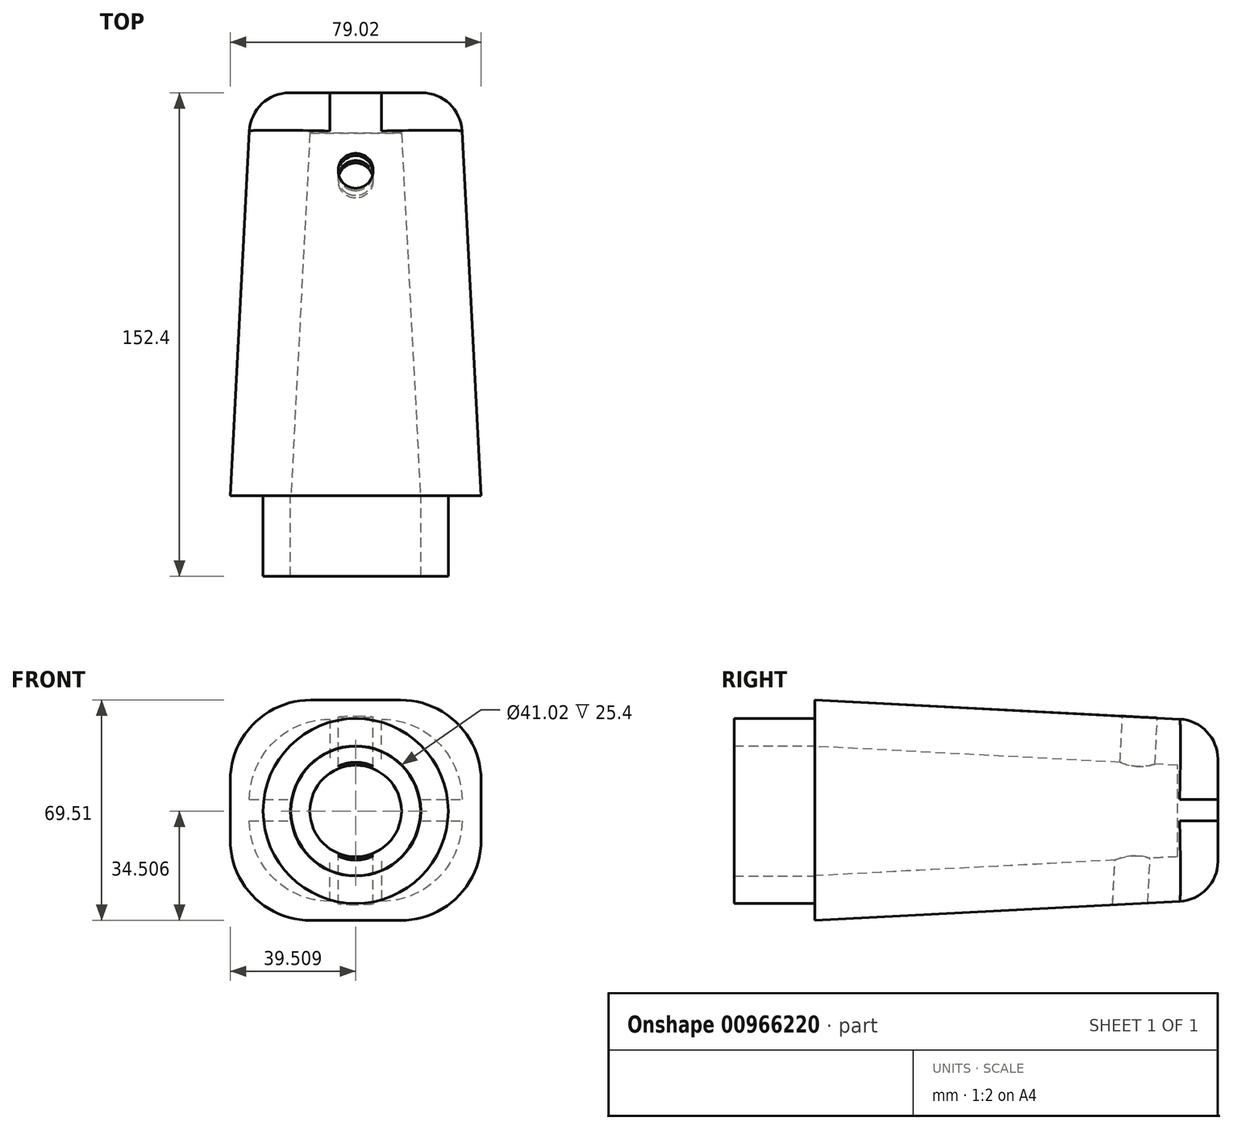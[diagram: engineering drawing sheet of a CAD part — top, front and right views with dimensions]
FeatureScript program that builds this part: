
annotation { "Feature Type Name" : "Feature", "Feature Type Description" : "" }
export const myFeature = defineFeature(function(context is Context, id is Id, definition is map)
    precondition{}
    {
        {
            var Q0;
            Q0=qCreatedBy(makeId("Front.planeOp"),FACE);
            var sketch = newSketch(context, id + "F0", { "sketchPlane" : qUnion([Q0])});
            skLineSegment(sketch, "E0.bottom", {"start": v(-78.57, 0) * mm, "end": v(-144.29, 0) * mm});
            skLineSegment(sketch, "E0.top", {"start": v(-78.57, 56.2) * mm, "end": v(-144.29, 56.2) * mm});
            skLineSegment(sketch, "E0.left", {"start": v(-78.57, 0) * mm, "end": v(-78.57, 56.2) * mm});
            skLineSegment(sketch, "E0.right", {"start": v(-144.29, 0) * mm, "end": v(-144.29, 56.2) * mm});
            skCircle(sketch, "E1", {"center": v(13.8, 21.63) * mm, "radius": 18.11 * mm, "construction": true});
            skSolve(sketch);
        }
        {
            var Q0;
            Q0=makeQuery(id+"F0.imprint","IMPRINT",FACE,{"disambiguationData":[TD([[makeQuery(id+"F0.imprint","IMPRINT",EDGE,{"derivedFrom":sQuery(id+"F0.wireOp",EDGE,"E0.bottom")}),-1.0]])]});
            extrude(context, id + "F1", {"entities" : qUnion([Q0]), "depth" : 127 * mm, "offsetDistance" : 25.4 * mm, "hasDraft" : true, "draftAngle" : 3 * degree});
        }
        {
            var Q0;
            Q0=makeQuery(id+"F1.opExtrude","SWEPT_EDGE",EDGE,{"disambiguationData":[OSD([sQuery(id+"F0.wireOp",EDGE,"E0.top"),sQuery(id+"F0.wireOp",EDGE,"E0.left")])]});
            var Q1;
            Q1=makeQuery(id+"F1.opExtrude","SWEPT_EDGE",EDGE,{"disambiguationData":[OSD([sQuery(id+"F0.wireOp",EDGE,"E0.top"),sQuery(id+"F0.wireOp",EDGE,"E0.right")])]});
            var Q2;
            Q2=makeQuery(id+"F1.opExtrude","SWEPT_EDGE",EDGE,{"disambiguationData":[OSD([sQuery(id+"F0.wireOp",EDGE,"E0.bottom"),sQuery(id+"F0.wireOp",EDGE,"E0.left")])]});
            var Q3;
            Q3=makeQuery(id+"F1.opExtrude","SWEPT_EDGE",EDGE,{"disambiguationData":[OSD([sQuery(id+"F0.wireOp",EDGE,"E0.bottom"),sQuery(id+"F0.wireOp",EDGE,"E0.right")])]});
            fillet(context, id + "F2", {"entities" : qUnion([Q0, Q1, Q2, Q3]), "radius" : 25.4 * mm, "tangentPropagation" : true, "allowEdgeOverflow" : false});
        }
        {
            var Q0;
            Q0=makeQuery(id+"F1.opExtrude","CAP_FACE",FACE,{"disambiguationData":[OSD([sQuery(id+"F0.wireOp",EDGE,"E0.bottom"),sQuery(id+"F0.wireOp",EDGE,"E0.top"),sQuery(id+"F0.wireOp",EDGE,"E0.left"),sQuery(id+"F0.wireOp",EDGE,"E0.right")])],"isStart":false});
            var sketch = newSketch(context, id + "F3", { "sketchPlane" : qUnion([Q0])});
            skCircle(sketch, "E2", {"center": v(-111.43, 27.85) * mm, "radius": 20.4 * mm});
            skPoint(sketch, "E2.centerSnap0", {"position": v(-111.43, 62.85) * mm});
            skSolve(sketch);
        }
        {
            var Q0;
            Q0=makeQuery(id+"F3.imprint","IMPRINT",FACE,{"disambiguationData":[TD([[makeQuery(id+"F3.imprint","IMPRINT",EDGE,{"derivedFrom":sQuery(id+"F3.wireOp",EDGE,"E2")}),1.0]])]});
            extrude(context, id + "F4", {"entities" : qUnion([Q0]), "operationType" : NewBodyOperationType.REMOVE, "oppositeDirection" : true, "depth" : 114.3 * mm, "offsetDistance" : 25.4 * mm, "hasDraft" : true, "draftAngle" : 3 * degree, "draftPullDirection" : true});
        }
        {
            var Q0;
            Q0=makeQuery(id+"F1.opExtrude","SWEPT_FACE",FACE,{"disambiguationData":[OSD([sQuery(id+"F0.wireOp",EDGE,"E0.top")])]});
            var sketch = newSketch(context, id + "F5", { "sketchPlane" : qUnion([Q0])});
            skPoint(sketch, "E3.centerSnap0", {"position": v(-111.43, -2.94) * mm});
            skCircle(sketch, "E4", {"center": v(-111.43, -27.53) * mm, "radius": 5.5 * mm});
            skSolve(sketch);
        }
        {
            var Q0;
            Q0=makeQuery(id+"F5.imprint","IMPRINT",FACE,{"disambiguationData":[TD([[makeQuery(id+"F5.imprint","IMPRINT",EDGE,{"derivedFrom":sQuery(id+"F5.wireOp",EDGE,"E4")}),1.0]])]});
            extrude(context, id + "F6", {"entities" : qUnion([Q0]), "operationType" : NewBodyOperationType.REMOVE, "oppositeDirection" : true, "depth" : 76.2 * mm, "offsetDistance" : 25.4 * mm});
        }
        {
            var Q0;
            {var subQ0=sQuery(id+"F0.wireOp",EDGE,"E0.right");var subQ1=sQuery(id+"F0.wireOp",EDGE,"E0.bottom");Q0=makeQuery(id+"F2.opFillet","BLEND_EDGE",EDGE,{"blendedFrom":[makeQuery(id+"F1.opExtrude","SWEPT_EDGE",EDGE,{"disambiguationData":[OSD([subQ1,subQ0])]}),makeQuery(id+"F1.opExtrude","CAP_FACE",FACE,{"disambiguationData":[OSD([subQ1,sQuery(id+"F0.wireOp",EDGE,"E0.top"),sQuery(id+"F0.wireOp",EDGE,"E0.left"),subQ0])],"isStart":true})],"blendedInto":[makeQuery(id+"F1.opExtrude","CAP_FACE",FACE,{"disambiguationData":[OSD([subQ1,sQuery(id+"F0.wireOp",EDGE,"E0.top"),sQuery(id+"F0.wireOp",EDGE,"E0.left"),subQ0])],"isStart":true})]});}
            fillet(context, id + "F7", {"entities" : qUnion([Q0]), "radius" : 12.7 * mm, "tangentPropagation" : true, "allowEdgeOverflow" : false});
        }
        {
            var Q0;
            Q0=makeQuery(id+"F1.opExtrude","CAP_FACE",FACE,{"disambiguationData":[OSD([sQuery(id+"F0.wireOp",EDGE,"E0.bottom"),sQuery(id+"F0.wireOp",EDGE,"E0.top"),sQuery(id+"F0.wireOp",EDGE,"E0.left"),sQuery(id+"F0.wireOp",EDGE,"E0.right")])],"isStart":false});
            var sketch = newSketch(context, id + "F8", { "sketchPlane" : qUnion([Q0])});
            skCircle(sketch, "E5", {"center": v(-111.43, 27.85) * mm, "radius": 29.15 * mm});
            skCircle(sketch, "E6", {"center": v(-111.43, 27.85) * mm, "radius": 20.51 * mm});
            skSolve(sketch);
        }
        {
            var Q0;
            Q0=makeQuery(id+"F8.imprint","IMPRINT",FACE,{"disambiguationData":[TD([[makeQuery(id+"F8.imprint","IMPRINT",EDGE,{"derivedFrom":sQuery(id+"F8.wireOp",EDGE,"E5")}),1.0]])]});
            extrude(context, id + "F9", {"entities" : qUnion([Q0]), "operationType" : NewBodyOperationType.ADD, "depth" : 25.4 * mm, "offsetDistance" : 25.4 * mm});
        }
    });
